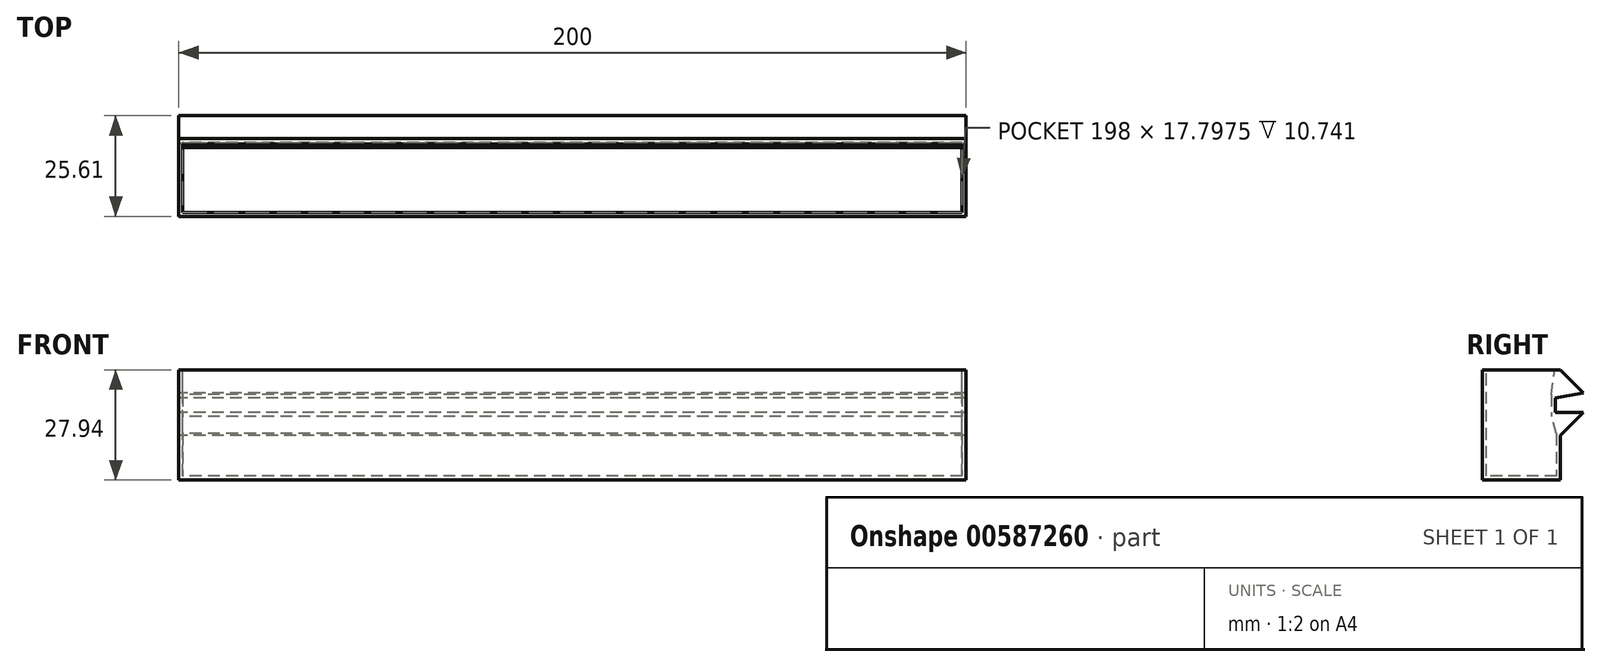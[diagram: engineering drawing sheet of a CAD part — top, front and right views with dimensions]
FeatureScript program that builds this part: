
annotation { "Feature Type Name" : "Feature", "Feature Type Description" : "" }
export const myFeature = defineFeature(function(context is Context, id is Id, definition is map)
    precondition{}
    {
        {
            var Q0;
            Q0=qCreatedBy(makeId("Right.planeOp"),FACE);
            var sketch = newSketch(context, id + "F0", { "sketchPlane" : qUnion([Q0])});
            skLineSegment(sketch, "E0", {"start": v(0, 1.81) * mm, "end": v(-1.32, 1.81) * mm});
            skLineSegment(sketch, "E1", {"start": v(-1.32, 1.81) * mm, "end": v(-1.32, 0.52) * mm});
            skLineSegment(sketch, "E2", {"start": v(-1.32, -3.19) * mm, "end": v(0, -3.19) * mm});
            skLineSegment(sketch, "E3", {"start": v(0, -3.19) * mm, "end": v(0, -20.32) * mm});
            skLineSegment(sketch, "E4", {"start": v(0, -20.32) * mm, "end": v(-19.8, -20.32) * mm});
            skLineSegment(sketch, "E5", {"start": v(-19.8, -20.32) * mm, "end": v(-19.8, 7.62) * mm});
            skLineSegment(sketch, "E6", {"start": v(-19.8, 7.62) * mm, "end": v(0, 7.62) * mm});
            skLineSegment(sketch, "E7", {"start": v(0, 7.62) * mm, "end": v(0, 1.81) * mm, "construction": true});
            skLineSegment(sketch, "E8", {"start": v(0, 7.62) * mm, "end": v(5.8, 1.81) * mm});
            skLineSegment(sketch, "E9", {"start": v(5.8, 1.81) * mm, "end": v(0, 1.81) * mm});
            skLineSegment(sketch, "E10", {"start": v(0, -3.19) * mm, "end": v(5.8, -3.19) * mm});
            skLineSegment(sketch, "E11", {"start": v(5.8, -3.19) * mm, "end": v(0, -9) * mm});
            skLineSegment(sketch, "E12", {"start": v(0, -9) * mm, "end": v(0, -3.19) * mm, "construction": true});
            skLineSegment(sketch, "E13", {"start": v(5.8, 1.81) * mm, "end": v(-1.32, 0.52) * mm});
            skLineSegment(sketch, "E14", {"start": v(-1.32, 0.52) * mm, "end": v(-1.32, -3.19) * mm});
            skSolve(sketch);
        }
        {
            var Q0;
            Q0 = qSketchRegion(id + "F0", true);
            extrude(context, id + "F1", {"entities" : qUnion([Q0]), "endBound" : BoundingType.SYMMETRIC, "depth" : 200 * mm, "offsetDistance" : 25 * mm});
        }
        {
            var Q0;
            Q0=makeQuery(id+"F1.opExtrude","SWEPT_FACE",FACE,{"disambiguationData":[OSD([sQuery(id+"F0.wireOp",EDGE,"E6")])]});
            shell(context, id + "F2", {"entities" : qUnion([Q0]), "thickness" : 1 * mm});
        }
        {
            var Q0;
            {var subQ0=sQuery(id+"F0.wireOp",EDGE,"E11");var subQ1=sQuery(id+"F0.wireOp",EDGE,"E10");var subQ2=sQuery(id+"F0.wireOp",EDGE,"E9");var subQ3=sQuery(id+"F0.wireOp",EDGE,"E8");var subQ4=sQuery(id+"F0.wireOp",EDGE,"E6");var subQ5=sQuery(id+"F0.wireOp",EDGE,"E5");var subQ6=sQuery(id+"F0.wireOp",EDGE,"E4");var subQ7=sQuery(id+"F0.wireOp",EDGE,"E3");var subQ8=sQuery(id+"F0.wireOp",EDGE,"E2");var subQ9=sQuery(id+"F0.wireOp",EDGE,"E1");var subQ10=sQuery(id+"F0.wireOp",EDGE,"E0");Q0=makeQuery(id+"F2.opShell","OFFSET_FACE",FACE,{"disambiguationData":[OSD([subQ10,subQ9,subQ8,subQ7,subQ6,subQ5,subQ4,subQ3,subQ2,subQ1,subQ0]),TDD([makeQuery(id+"F1.opExtrude","CAP_FACE",FACE,{"disambiguationData":[OSD([subQ10,subQ9,subQ8,subQ7,subQ6,subQ5,subQ4,subQ3,subQ2,subQ1,subQ0])],"isStart":true})])]});}
            var sketch = newSketch(context, id + "F3", { "sketchPlane" : qUnion([Q0])});
            skLineSegment(sketch, "E15", {"start": v(-2.32, 1.35) * mm, "end": v(-1.41, 7.62) * mm});
            skLineSegment(sketch, "E16", {"start": v(-1, -8.58) * mm, "end": v(-2.32, -4.19) * mm});
            skSolve(sketch);
        }
        {
            var Q0;
            Q0 = qSketchRegion(id + "F3", true);
            var Q1;
            Q1=makeQuery(id+"F3.imprint","IMPRINT",FACE,{"disambiguationData":[TD([[makeQuery(id+"F3.imprint","IMPRINT",EDGE,{"derivedFrom":sQuery(id+"F3.wireOp",EDGE,"E15")}),-1.0]])]});
            var Q2;
            Q2=makeQuery(id+"F3.imprint","IMPRINT",FACE,{"disambiguationData":[TD([[makeQuery(id+"F3.imprint","IMPRINT",EDGE,{"derivedFrom":sQuery(id+"F3.wireOp",EDGE,"E16")}),-1.0]])]});
            extrude(context, id + "F4", {"entities" : qUnion([Q0, Q1, Q2]), "operationType" : NewBodyOperationType.ADD, "endBound" : BoundingType.UP_TO_NEXT, "depth" : 25 * mm, "offsetDistance" : 25 * mm});
        }
    });
